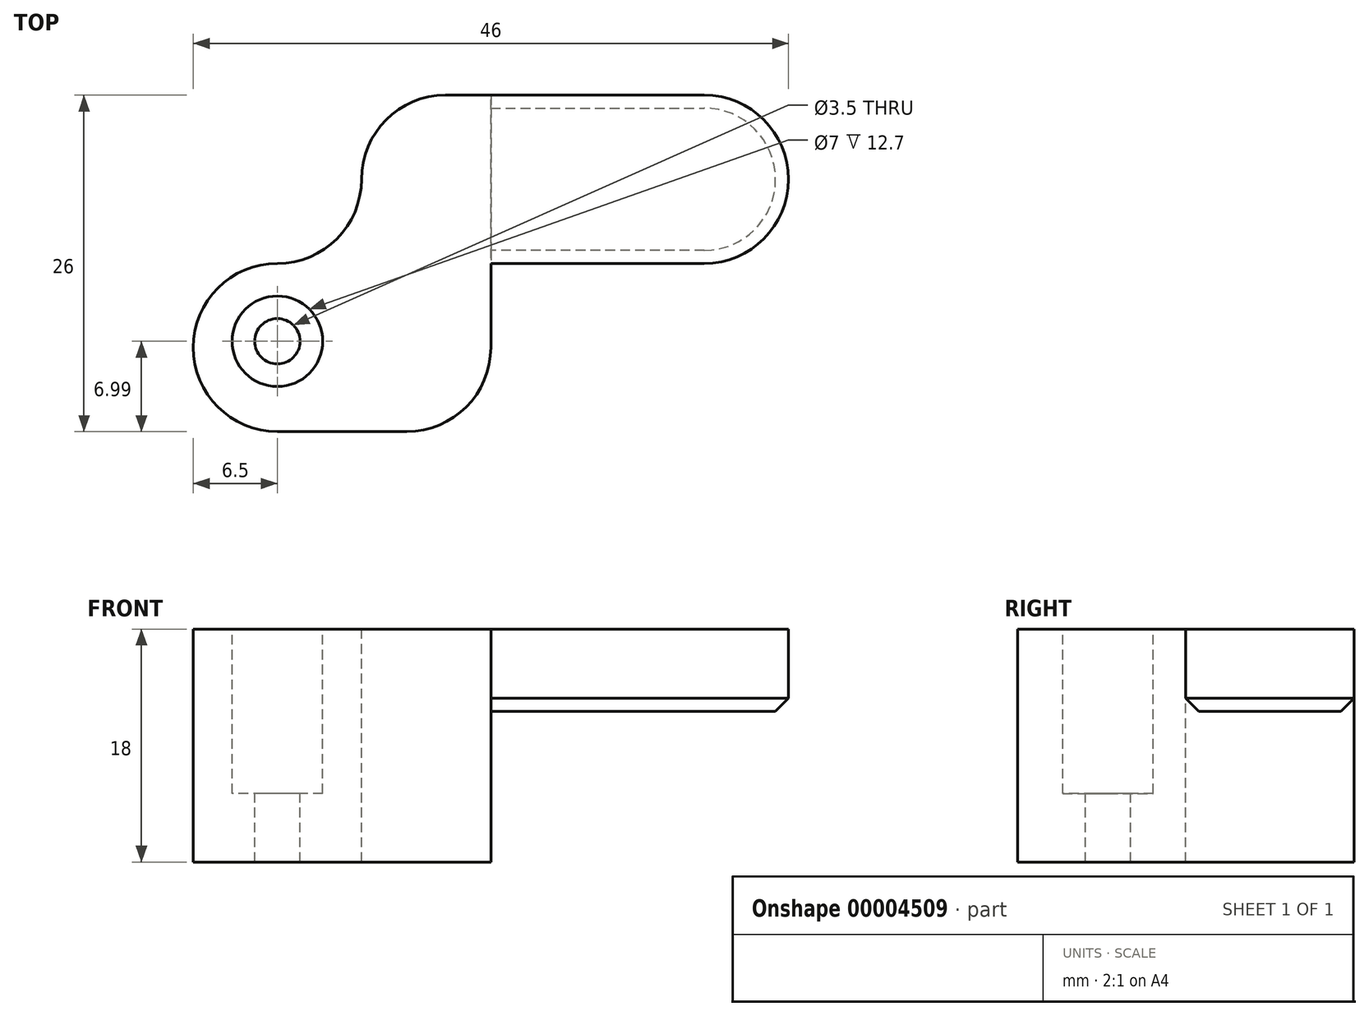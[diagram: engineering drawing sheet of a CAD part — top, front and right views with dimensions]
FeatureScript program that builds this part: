
annotation { "Feature Type Name" : "Feature", "Feature Type Description" : "" }
export const myFeature = defineFeature(function(context is Context, id is Id, definition is map)
    precondition{}
    {
        {
            var Q0;
            Q0=qCreatedBy(makeId("Top.planeOp"),FACE);
            var sketch = newSketch(context, id + "F0", { "sketchPlane" : qUnion([Q0])});
            skLineSegment(sketch, "E0", {"start": v(-23, 6.01) * mm, "end": v(-23, -6.99) * mm});
            skLineSegment(sketch, "E1", {"start": v(-23, -6.99) * mm, "end": v(0, -6.99) * mm});
            skLineSegment(sketch, "E2", {"start": v(0, -6.99) * mm, "end": v(0, 19.01) * mm});
            skLineSegment(sketch, "E3", {"start": v(0, 19.01) * mm, "end": v(-10, 19.01) * mm});
            skLineSegment(sketch, "E4", {"start": v(-10, 19.01) * mm, "end": v(-10, 6.01) * mm});
            skLineSegment(sketch, "E5", {"start": v(-10, 6.01) * mm, "end": v(-23, 6.01) * mm});
            skSolve(sketch);
        }
        {
            var Q0;
            Q0=makeQuery(id+"F0.imprint","IMPRINT",FACE,{"disambiguationData":[TD([[makeQuery(id+"F0.imprint","IMPRINT",EDGE,{"derivedFrom":sQuery(id+"F0.wireOp",EDGE,"E0")}),1.0]])]});
            extrude(context, id + "F1", {"entities" : qUnion([Q0]), "oppositeDirection" : true, "depth" : 18 * mm});
        }
        {
            var Q0;
            Q0=qCreatedBy(makeId("Top.planeOp"),FACE);
            var sketch = newSketch(context, id + "F2", { "sketchPlane" : qUnion([Q0])});
            skPoint(sketch, "E6.0", {"position": v(0, 19.01) * mm});
            skLineSegment(sketch, "E7.bottom", {"start": v(0, 19.01) * mm, "end": v(23, 19.01) * mm});
            skLineSegment(sketch, "E7.top", {"start": v(0, 6.01) * mm, "end": v(23, 6.01) * mm});
            skLineSegment(sketch, "E7.left", {"start": v(0, 19.01) * mm, "end": v(0, 6.01) * mm});
            skLineSegment(sketch, "E7.right", {"start": v(23, 19.01) * mm, "end": v(23, 6.01) * mm});
            skSolve(sketch);
        }
        {
            var Q0;
            Q0 = qSketchRegion(id + "F2", true);
            extrude(context, id + "F3", {"entities" : qUnion([Q0]), "operationType" : NewBodyOperationType.ADD, "oppositeDirection" : true, "depth" : 6.35 * mm});
        }
        {
            var Q0;
            Q0=qCreatedBy(makeId("Top.planeOp"),FACE);
            var sketch = newSketch(context, id + "F4", { "sketchPlane" : qUnion([Q0])});
            skCircle(sketch, "E8", {"center": v(-16.5, 0) * mm, "radius": 1.75 * mm});
            skSolve(sketch);
        }
        {
            var Q0;
            Q0 = qSketchRegion(id + "F4", true);
            extrude(context, id + "F5", {"entities" : qUnion([Q0]), "operationType" : NewBodyOperationType.REMOVE, "endBound" : BoundingType.THROUGH_ALL, "oppositeDirection" : true, "depth" : 25 * mm});
        }
        {
            var Q0;
            Q0=qCreatedBy(makeId("Top.planeOp"),FACE);
            var sketch = newSketch(context, id + "F6", { "sketchPlane" : qUnion([Q0])});
            skCircle(sketch, "E9", {"center": v(-16.5, 0) * mm, "radius": 3.5 * mm});
            skSolve(sketch);
        }
        {
            var Q0;
            Q0 = qSketchRegion(id + "F6", true);
            extrude(context, id + "F7", {"entities" : qUnion([Q0]), "operationType" : NewBodyOperationType.REMOVE, "oppositeDirection" : true, "depth" : 12.7 * mm});
        }
        {
            var Q0;
            Q0=makeQuery(id+"F3.opExtrude","SWEPT_EDGE",EDGE,{"disambiguationData":[OSD([sQuery(id+"F2.wireOp",EDGE,"E7.top"),sQuery(id+"F2.wireOp",EDGE,"E7.left")])]});
            var Q1;
            Q1=makeQuery(id+"F3.opExtrude","SWEPT_EDGE",EDGE,{"disambiguationData":[OSD([sQuery(id+"F2.wireOp",EDGE,"E7.bottom"),sQuery(id+"F2.wireOp",EDGE,"E7.right")])]});
            var Q2;
            Q2=makeQuery(id+"F3.opExtrude","SWEPT_EDGE",EDGE,{"disambiguationData":[OSD([sQuery(id+"F2.wireOp",EDGE,"E7.top"),sQuery(id+"F2.wireOp",EDGE,"E7.right")])]});
            fillet(context, id + "F8", {"entities" : qUnion([Q0, Q1, Q2]), "radius" : 6.5 * mm, "tangentPropagation" : true, "allowEdgeOverflow" : false});
        }
        {
            var Q0;
            {var subQ0=sQuery(id+"F2.wireOp",EDGE,"E7.bottom");var subQ1=sQuery(id+"F2.wireOp",EDGE,"E7.right");Q0=makeQuery(id+"F8.opFillet","BLEND_EDGE",EDGE,{"blendedFrom":[makeQuery(id+"F3.opExtrude","SWEPT_EDGE",EDGE,{"disambiguationData":[OSD([subQ0,subQ1])]}),makeQuery(id+"F3.opExtrude","CAP_FACE",FACE,{"disambiguationData":[OSD([subQ0,sQuery(id+"F2.wireOp",EDGE,"E7.top"),sQuery(id+"F2.wireOp",EDGE,"E7.left"),subQ1])],"isStart":false})],"blendedInto":[makeQuery(id+"F3.opExtrude","CAP_FACE",FACE,{"disambiguationData":[OSD([subQ0,sQuery(id+"F2.wireOp",EDGE,"E7.top"),sQuery(id+"F2.wireOp",EDGE,"E7.left"),subQ1])],"isStart":false})]});}
            chamfer(context, id + "F9", {"entities" : qUnion([Q0]), "width" : 1 * mm, "tangentPropagation" : true});
        }
        {
            var Q0;
            Q0=makeQuery(id+"F1.opExtrude","SWEPT_EDGE",EDGE,{"disambiguationData":[OSD([sQuery(id+"F0.wireOp",EDGE,"E1"),sQuery(id+"F0.wireOp",EDGE,"E2")])]});
            var Q1;
            Q1=makeQuery(id+"F1.opExtrude","SWEPT_EDGE",EDGE,{"disambiguationData":[OSD([sQuery(id+"F0.wireOp",EDGE,"E0"),sQuery(id+"F0.wireOp",EDGE,"E1")])]});
            var Q2;
            Q2=makeQuery(id+"F1.opExtrude","SWEPT_EDGE",EDGE,{"disambiguationData":[OSD([sQuery(id+"F0.wireOp",EDGE,"E0"),sQuery(id+"F0.wireOp",EDGE,"E5")])]});
            var Q3;
            Q3=makeQuery(id+"F1.opExtrude","SWEPT_EDGE",EDGE,{"disambiguationData":[OSD([sQuery(id+"F0.wireOp",EDGE,"E4"),sQuery(id+"F0.wireOp",EDGE,"E5")])]});
            var Q4;
            Q4=makeQuery(id+"F1.opExtrude","SWEPT_EDGE",EDGE,{"disambiguationData":[OSD([sQuery(id+"F0.wireOp",EDGE,"E3"),sQuery(id+"F0.wireOp",EDGE,"E4")])]});
            fillet(context, id + "F10", {"entities" : qUnion([Q0, Q1, Q2, Q3, Q4]), "radius" : 6.5 * mm, "tangentPropagation" : true, "allowEdgeOverflow" : false});
        }
    });
